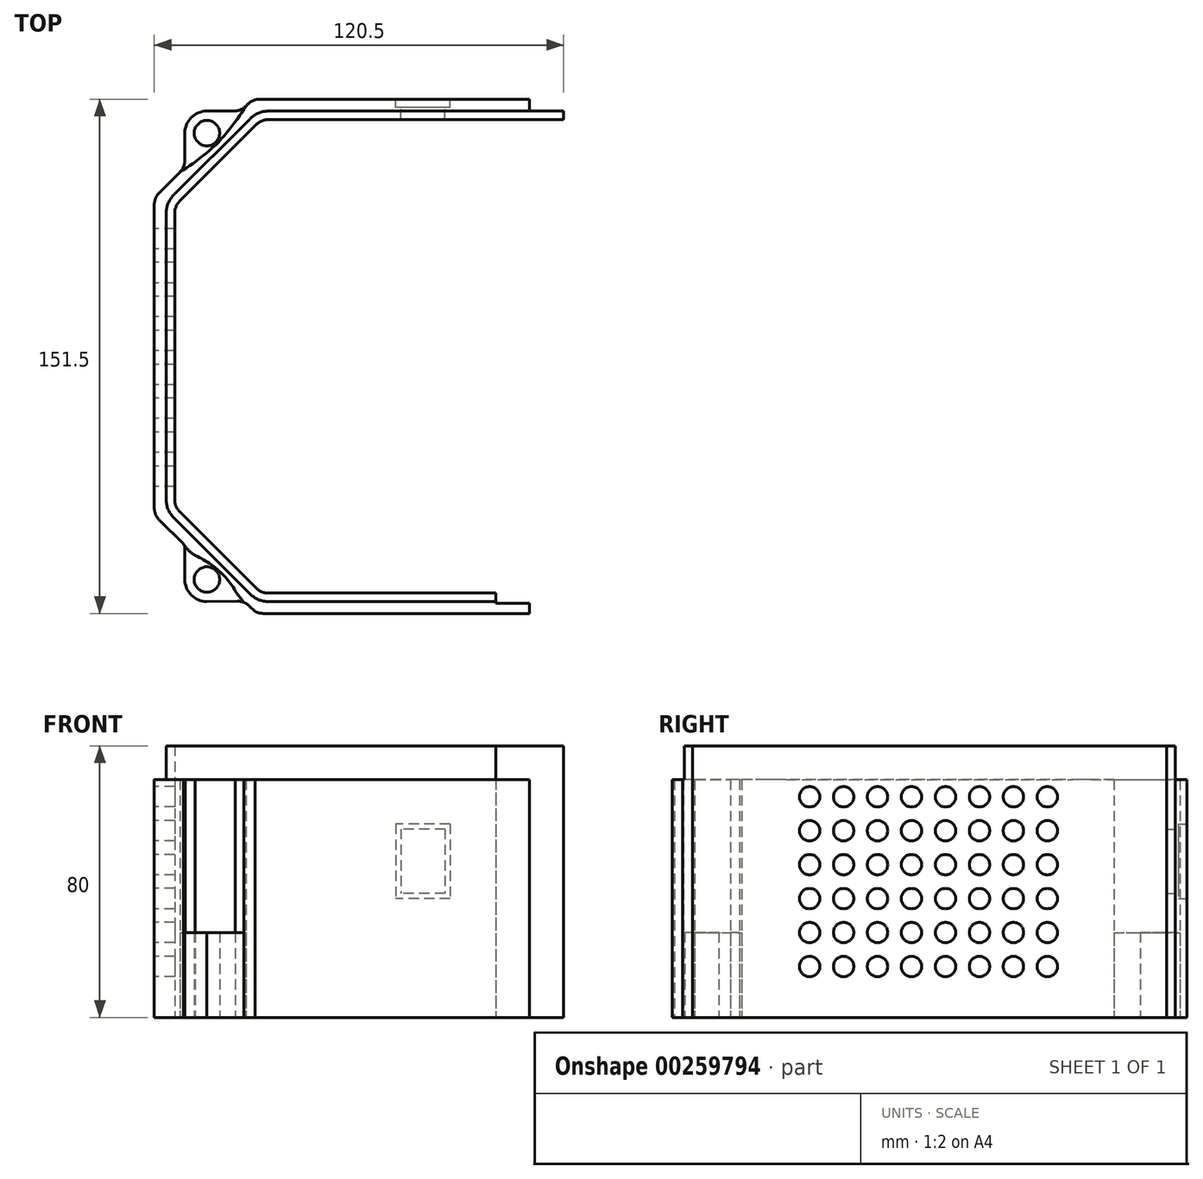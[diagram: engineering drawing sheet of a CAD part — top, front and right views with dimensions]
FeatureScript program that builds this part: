
annotation { "Feature Type Name" : "Feature", "Feature Type Description" : "" }
export const myFeature = defineFeature(function(context is Context, id is Id, definition is map)
    precondition{}
    {
        {
            var Q0;
            Q0=qCreatedBy(makeId("Top.planeOp"),FACE);
            var sketch = newSketch(context, id + "F0", { "sketchPlane" : qUnion([Q0])});
            skLineSegment(sketch, "E0.bottom", {"start": v(-49.42, 75.75) * mm, "end": v(30, 75.75) * mm});
            skLineSegment(sketch, "E0.top", {"start": v(-48.4, -75.75) * mm, "end": v(30, -75.75) * mm});
            skLineSegment(sketch, "E0.left", {"start": v(-80.5, 44.67) * mm, "end": v(-80.5, -44.67) * mm});
            skLineSegment(sketch, "E0.right", {"start": v(30, 75.75) * mm, "end": v(30, 72.25) * mm});
            skCircle(sketch, "E1", {"center": v(-65, 65.75) * mm, "radius": 3.75 * mm});
            skCircle(sketch, "E2", {"center": v(-65, -65.75) * mm, "radius": 3.75 * mm});
            skPoint(sketch, "E3.visualSharp", {"position": v(-80.5, 75.75) * mm});
            skPoint(sketch, "E4.visualSharp", {"position": v(-80.5, -75.75) * mm});
            skLineSegment(sketch, "E5.0", {"start": v(-46.93, 69.75) * mm, "end": v(30, 69.75) * mm});
            skLineSegment(sketch, "E6.trimOffspring", {"start": v(30, -72.75) * mm, "end": v(30, -75.75) * mm});
            skLineSegment(sketch, "E7", {"start": v(-73.04, 45.72) * mm, "end": v(-50.47, 68.29) * mm});
            skLineSegment(sketch, "E8", {"start": v(-73.04, -45.72) * mm, "end": v(-50.47, -68.29) * mm});
            skLineSegment(sketch, "E9.trimOffspring", {"start": v(-46.94, -69.75) * mm, "end": v(20, -69.75) * mm});
            skArc(sketch, "E10.trimOffspring", {"start": v(-60.05, -58.7) * mm, "mid": v(-60.25, -58.5) * mm, "end": v(-60.46, -58.3) * mm, "construction": true});
            skArc(sketch, "E11", {"start": v(-71.5, -65.75) * mm, "mid": v(-69.6, -70.35) * mm, "end": v(-65, -72.25) * mm});
            skArc(sketch, "E12", {"start": v(-65, 72.25) * mm, "mid": v(-69.6, 70.35) * mm, "end": v(-71.5, 65.75) * mm});
            skPoint(sketch, "E13.visualSharp", {"position": v(-49, -69.75) * mm});
            skArc(sketch, "E13.filletArc", {"start": v(-50.47, -68.29) * mm, "mid": v(-48.85, -69.37) * mm, "end": v(-46.94, -69.75) * mm});
            skPoint(sketch, "E14.visualSharp", {"position": v(-74.5, -44.26) * mm});
            skArc(sketch, "E14.filletArc", {"start": v(-74.5, -42.19) * mm, "mid": v(-74.12, -44.1) * mm, "end": v(-73.04, -45.72) * mm});
            skPoint(sketch, "E15.visualSharp", {"position": v(-74.5, 44.25) * mm});
            skArc(sketch, "E15.filletArc", {"start": v(-73.04, 45.72) * mm, "mid": v(-74.12, 44.1) * mm, "end": v(-74.5, 42.18) * mm});
            skPoint(sketch, "E16.visualSharp", {"position": v(-49, 69.75) * mm});
            skArc(sketch, "E16.filletArc", {"start": v(-46.93, 69.75) * mm, "mid": v(-48.85, 69.37) * mm, "end": v(-50.47, 68.29) * mm});
            skLineSegment(sketch, "E17", {"start": v(-79.04, -48.2) * mm, "end": v(-71.96, -55.28) * mm});
            skPoint(sketch, "E18.visualSharp", {"position": v(-70.5, -56.75) * mm});
            skArc(sketch, "E19.filletArc", {"start": v(-80.5, -44.67) * mm, "mid": v(-80.12, -46.59) * mm, "end": v(-79.04, -48.2) * mm});
            skPoint(sketch, "E20.visualSharp", {"position": v(-56, -71.25) * mm});
            skPoint(sketch, "E21.visualSharp", {"position": v(-51.5, -75.75) * mm});
            skArc(sketch, "E21.filletArc", {"start": v(-50.86, -75.1) * mm, "mid": v(-49.68, -75.59) * mm, "end": v(-48.4, -75.75) * mm});
            skLineSegment(sketch, "E22", {"start": v(-65, 72.25) * mm, "end": v(-57.06, 72.25) * mm});
            skLineSegment(sketch, "E23", {"start": v(-71.5, 57.81) * mm, "end": v(-71.5, 65.75) * mm});
            skLineSegment(sketch, "E24", {"start": v(-72.96, 54.28) * mm, "end": v(-79.04, 48.2) * mm});
            skLineSegment(sketch, "E25", {"start": v(-53.53, 73.71) * mm, "end": v(-52.95, 74.29) * mm});
            skPoint(sketch, "E26.visualSharp", {"position": v(-80.5, 46.74) * mm});
            skArc(sketch, "E26.filletArc", {"start": v(-79.04, 48.2) * mm, "mid": v(-80.12, 46.58) * mm, "end": v(-80.5, 44.67) * mm});
            skPoint(sketch, "E27.visualSharp", {"position": v(-71.5, 55.74) * mm});
            skArc(sketch, "E27.filletArc", {"start": v(-72.96, 54.28) * mm, "mid": v(-71.88, 55.9) * mm, "end": v(-71.5, 57.81) * mm});
            skPoint(sketch, "E28.visualSharp", {"position": v(-54.99, 72.25) * mm});
            skArc(sketch, "E28.filletArc", {"start": v(-57.06, 72.25) * mm, "mid": v(-55.15, 72.63) * mm, "end": v(-53.53, 73.71) * mm});
            skPoint(sketch, "E29.visualSharp", {"position": v(-51.49, 75.75) * mm});
            skArc(sketch, "E29.filletArc", {"start": v(-49.42, 75.75) * mm, "mid": v(-51.33, 75.37) * mm, "end": v(-52.95, 74.29) * mm});
            skLineSegment(sketch, "E30", {"start": v(-74.5, -42.19) * mm, "end": v(-74.5, 42.18) * mm});
            skLineSegment(sketch, "E31", {"start": v(-59, -59.75) * mm, "end": v(-80.03, -80.78) * mm, "construction": true});
            skArc(sketch, "E32.filletArc", {"start": v(-71.36, -56.02) * mm, "mid": v(-70.06, -57.5) * mm, "end": v(-68.44, -58.62) * mm});
            skPoint(sketch, "E33.orphan", {"position": v(-62.35, -63.1) * mm});
            skPoint(sketch, "E34.orphan", {"position": v(-56, -69.45) * mm});
            skPoint(sketch, "E35.orphan", {"position": v(-68.7, -56.75) * mm});
            skPoint(sketch, "E36", {"position": v(-62, -62.74) * mm});
            skFitSpline(sketch, "E37", {"points": [v(-56.66, -69.17) * mm, v(-62, -62.74) * mm, v(-68.44, -58.62) * mm], "startDerivative": vector(-7.08, 14.05) * mm, "endDerivative": vector(-14.05, 7.08) * mm});
            skLineSegment(sketch, "E38", {"start": v(-62, 62.74) * mm, "end": v(-62.35, 63.1) * mm, "construction": true});
            skPoint(sketch, "E39", {"position": v(-62, 62.74) * mm});
            skFitSpline(sketch, "E40", {"points": [v(-72.96, 54.28) * mm, v(-62, 62.74) * mm, v(-53.53, 73.71) * mm], "startDerivative": vector(21.19, 13.69) * mm, "endDerivative": vector(13.69, 21.19) * mm});
            skLineSegment(sketch, "E41.trimOffspring", {"start": v(-67.65, 68.4) * mm, "end": v(-69.6, 70.35) * mm, "construction": true});
            skLineSegment(sketch, "E42", {"start": v(-71.97, -55.28) * mm, "end": v(-71.96, -55.28) * mm});
            skLineSegment(sketch, "E43", {"start": v(-71.5, -65.75) * mm, "end": v(-71.5, -56.56) * mm});
            skLineSegment(sketch, "E44", {"start": v(-65, -72.25) * mm, "end": v(-56.04, -72.14) * mm});
            skArc(sketch, "E45.filletArc", {"start": v(-71.5, -56.56) * mm, "mid": v(-71.62, -55.88) * mm, "end": v(-71.97, -55.28) * mm});
            skLineSegment(sketch, "E46", {"start": v(-50.86, -75.1) * mm, "end": v(-52.55, -73.51) * mm});
            skPoint(sketch, "E47.visualSharp", {"position": v(-54.02, -72.12) * mm});
            skArc(sketch, "E47.filletArc", {"start": v(-52.55, -73.51) * mm, "mid": v(-54.16, -72.49) * mm, "end": v(-56.04, -72.14) * mm});
            skLineSegment(sketch, "E48", {"start": v(-56.66, -69.17) * mm, "end": v(-54.16, -72.49) * mm});
            skLineSegment(sketch, "E49", {"start": v(-71.36, -56.02) * mm, "end": v(-71.96, -55.28) * mm});
            skLineSegment(sketch, "E50.bottom", {"start": v(30, 69.75) * mm, "end": v(40, 69.75) * mm});
            skLineSegment(sketch, "E50.top", {"start": v(30, 72.25) * mm, "end": v(40, 72.25) * mm});
            skLineSegment(sketch, "E50.right", {"start": v(40, 69.75) * mm, "end": v(40, 72.25) * mm});
            skLineSegment(sketch, "E51.top", {"start": v(20, -72.75) * mm, "end": v(30, -72.75) * mm});
            skLineSegment(sketch, "E51.left", {"start": v(20, -69.75) * mm, "end": v(20, -72.75) * mm});
            skSolve(sketch);
        }
        {
            var Q0;
            Q0=makeQuery(id+"F0.imprint","IMPRINT",FACE,{"disambiguationData":[TD([[makeQuery(id+"F0.imprint","IMPRINT",EDGE,{"derivedFrom":sQuery(id+"F0.wireOp",EDGE,"E2")}),-1.0]])]});
            var Q1;
            Q1=makeQuery(id+"F0.imprint","IMPRINT",FACE,{"disambiguationData":[TD([[makeQuery(id+"F0.imprint","IMPRINT",EDGE,{"derivedFrom":sQuery(id+"F0.wireOp",EDGE,"E1")}),-1.0]])]});
            extrude(context, id + "F1", {"entities" : qUnion([Q0, Q1]), "depth" : 25 * mm});
        }
        {
            var Q0;
            Q0=makeQuery(id+"F0.imprint","IMPRINT",FACE,{"disambiguationData":[TD([[makeQuery(id+"F0.imprint","IMPRINT",EDGE,{"derivedFrom":sQuery(id+"F0.wireOp",EDGE,"E0.bottom")}),-1.0]])]});
            extrude(context, id + "F2", {"entities" : qUnion([Q0]), "depth" : 70 * mm});
        }
        {
            var Q0;
            Q0=makeQuery(id+"F2.opExtrude","CAP_FACE",FACE,{"disambiguationData":[OSD([sQuery(id+"F0.wireOp",EDGE,"E0.bottom"),sQuery(id+"F0.wireOp",EDGE,"E0.top"),sQuery(id+"F0.wireOp",EDGE,"E0.left"),sQuery(id+"F0.wireOp",EDGE,"E0.right"),sQuery(id+"F0.wireOp",EDGE,"E5.0"),sQuery(id+"F0.wireOp",EDGE,"E6.trimOffspring"),sQuery(id+"F0.wireOp",EDGE,"E7"),sQuery(id+"F0.wireOp",EDGE,"E8"),sQuery(id+"F0.wireOp",EDGE,"E9.trimOffspring"),sQuery(id+"F0.wireOp",EDGE,"E13.filletArc"),sQuery(id+"F0.wireOp",EDGE,"E14.filletArc"),sQuery(id+"F0.wireOp",EDGE,"E15.filletArc"),sQuery(id+"F0.wireOp",EDGE,"E16.filletArc"),sQuery(id+"F0.wireOp",EDGE,"E17"),sQuery(id+"F0.wireOp",EDGE,"E19.filletArc"),sQuery(id+"F0.wireOp",EDGE,"E21.filletArc"),sQuery(id+"F0.wireOp",EDGE,"E24"),sQuery(id+"F0.wireOp",EDGE,"E25"),sQuery(id+"F0.wireOp",EDGE,"E26.filletArc"),sQuery(id+"F0.wireOp",EDGE,"E29.filletArc"),sQuery(id+"F0.wireOp",EDGE,"E30"),sQuery(id+"F0.wireOp",EDGE,"E32.filletArc"),sQuery(id+"F0.wireOp",EDGE,"E37"),sQuery(id+"F0.wireOp",EDGE,"E40"),sQuery(id+"F0.wireOp",EDGE,"E46"),sQuery(id+"F0.wireOp",EDGE,"E47.filletArc"),sQuery(id+"F0.wireOp",EDGE,"E48"),sQuery(id+"F0.wireOp",EDGE,"E49"),sQuery(id+"F0.wireOp",EDGE,"E50.bottom"),sQuery(id+"F0.wireOp",EDGE,"E50.top"),sQuery(id+"F0.wireOp",EDGE,"E50.right"),sQuery(id+"F0.wireOp",EDGE,"E51.top"),sQuery(id+"F0.wireOp",EDGE,"E51.left")])],"isStart":false});
            var sketch = newSketch(context, id + "F3", { "sketchPlane" : qUnion([Q0])});
            skLineSegment(sketch, "E52.0", {"start": v(-46.94, -72.25) * mm, "end": v(20, -72.25) * mm});
            skArc(sketch, "E52.1", {"start": v(-52.24, -70.05) * mm, "mid": v(-49.8, -71.68) * mm, "end": v(-46.94, -72.25) * mm});
            skLineSegment(sketch, "E52.2", {"start": v(-74.8, -47.5) * mm, "end": v(-52.24, -70.05) * mm});
            skArc(sketch, "E52.3", {"start": v(-77, -42.19) * mm, "mid": v(-76.43, -45.06) * mm, "end": v(-74.8, -47.5) * mm});
            skLineSegment(sketch, "E52.4", {"start": v(-77, -42.19) * mm, "end": v(-77, 42.18) * mm});
            skArc(sketch, "E52.5", {"start": v(-74.8, 47.49) * mm, "mid": v(-76.43, 45.05) * mm, "end": v(-77, 42.18) * mm});
            skLineSegment(sketch, "E52.6", {"start": v(30, 72.25) * mm, "end": v(40, 72.25) * mm});
            skLineSegment(sketch, "E52.7", {"start": v(-46.93, 72.25) * mm, "end": v(30, 72.25) * mm});
            skArc(sketch, "E52.8", {"start": v(-46.93, 72.25) * mm, "mid": v(-49.8, 71.68) * mm, "end": v(-52.24, 70.05) * mm});
            skLineSegment(sketch, "E52.9", {"start": v(-74.8, 47.49) * mm, "end": v(-52.24, 70.05) * mm});
            skLineSegment(sketch, "E53", {"start": v(20, -72.25) * mm, "end": v(20, -69.75) * mm});
            skLineSegment(sketch, "E54", {"start": v(40, 69.75) * mm, "end": v(40, 72.25) * mm});
            skSolve(sketch);
        }
        {
            var Q0;
            Q0=makeQuery(id+"F3.imprint","IMPRINT",FACE,{"disambiguationData":[TD([[makeQuery(id+"F3.imprint","IMPRINT",EDGE,{"derivedFrom":sQuery(id+"F3.wireOp",EDGE,"E52.0")}),1.0]])]});
            extrude(context, id + "F4", {"entities" : qUnion([Q0]), "operationType" : NewBodyOperationType.ADD, "depth" : 10 * mm});
        }
        {
            var Q0;
            Q0=makeQuery(id+"F2.opExtrude","SWEPT_FACE",FACE,{"disambiguationData":[OSD([sQuery(id+"F0.wireOp",EDGE,"E0.left")])]});
            var sketch = newSketch(context, id + "F5", { "sketchPlane" : qUnion([Q0])});
            skCircle(sketch, "E55", {"center": v(-34.67, 15) * mm, "radius": 3 * mm});
            skCircle(sketch, "E56.0.1.0", {"center": v(-34.67, 25) * mm, "radius": 3 * mm});
            skCircle(sketch, "E56.0.2.0", {"center": v(-34.67, 35) * mm, "radius": 3 * mm});
            skCircle(sketch, "E56.0.3.0", {"center": v(-34.67, 45) * mm, "radius": 3 * mm});
            skCircle(sketch, "E56.0.4.0", {"center": v(-34.67, 55) * mm, "radius": 3 * mm});
            skCircle(sketch, "E56.0.5.0", {"center": v(-34.67, 65) * mm, "radius": 3 * mm});
            skCircle(sketch, "E56.1.0.0", {"center": v(-24.67, 15) * mm, "radius": 3 * mm});
            skCircle(sketch, "E56.1.1.0", {"center": v(-24.67, 25) * mm, "radius": 3 * mm});
            skCircle(sketch, "E56.1.2.0", {"center": v(-24.67, 35) * mm, "radius": 3 * mm});
            skCircle(sketch, "E56.1.3.0", {"center": v(-24.67, 45) * mm, "radius": 3 * mm});
            skCircle(sketch, "E56.1.4.0", {"center": v(-24.67, 55) * mm, "radius": 3 * mm});
            skCircle(sketch, "E56.1.5.0", {"center": v(-24.67, 65) * mm, "radius": 3 * mm});
            skCircle(sketch, "E56.2.0.0", {"center": v(-14.67, 15) * mm, "radius": 3 * mm});
            skCircle(sketch, "E56.2.1.0", {"center": v(-14.67, 25) * mm, "radius": 3 * mm});
            skCircle(sketch, "E56.2.2.0", {"center": v(-14.67, 35) * mm, "radius": 3 * mm});
            skCircle(sketch, "E56.2.3.0", {"center": v(-14.67, 45) * mm, "radius": 3 * mm});
            skCircle(sketch, "E56.2.4.0", {"center": v(-14.67, 55) * mm, "radius": 3 * mm});
            skCircle(sketch, "E56.2.5.0", {"center": v(-14.67, 65) * mm, "radius": 3 * mm});
            skCircle(sketch, "E56.3.0.0", {"center": v(-4.67, 15) * mm, "radius": 3 * mm});
            skCircle(sketch, "E56.3.1.0", {"center": v(-4.67, 25) * mm, "radius": 3 * mm});
            skCircle(sketch, "E56.3.2.0", {"center": v(-4.67, 35) * mm, "radius": 3 * mm});
            skCircle(sketch, "E56.3.3.0", {"center": v(-4.67, 45) * mm, "radius": 3 * mm});
            skCircle(sketch, "E56.3.4.0", {"center": v(-4.67, 55) * mm, "radius": 3 * mm});
            skCircle(sketch, "E56.3.5.0", {"center": v(-4.67, 65) * mm, "radius": 3 * mm});
            skCircle(sketch, "E56.4.0.0", {"center": v(5.33, 15) * mm, "radius": 3 * mm});
            skCircle(sketch, "E56.4.1.0", {"center": v(5.33, 25) * mm, "radius": 3 * mm});
            skCircle(sketch, "E56.4.2.0", {"center": v(5.33, 35) * mm, "radius": 3 * mm});
            skCircle(sketch, "E56.4.3.0", {"center": v(5.33, 45) * mm, "radius": 3 * mm});
            skCircle(sketch, "E56.4.4.0", {"center": v(5.33, 55) * mm, "radius": 3 * mm});
            skCircle(sketch, "E56.4.5.0", {"center": v(5.33, 65) * mm, "radius": 3 * mm});
            skCircle(sketch, "E56.5.0.0", {"center": v(15.33, 15) * mm, "radius": 3 * mm});
            skCircle(sketch, "E56.5.1.0", {"center": v(15.33, 25) * mm, "radius": 3 * mm});
            skCircle(sketch, "E56.5.2.0", {"center": v(15.33, 35) * mm, "radius": 3 * mm});
            skCircle(sketch, "E56.5.3.0", {"center": v(15.33, 45) * mm, "radius": 3 * mm});
            skCircle(sketch, "E56.5.4.0", {"center": v(15.33, 55) * mm, "radius": 3 * mm});
            skCircle(sketch, "E56.5.5.0", {"center": v(15.33, 65) * mm, "radius": 3 * mm});
            skCircle(sketch, "E56.6.0.0", {"center": v(25.33, 15) * mm, "radius": 3 * mm});
            skCircle(sketch, "E56.6.1.0", {"center": v(25.33, 25) * mm, "radius": 3 * mm});
            skCircle(sketch, "E56.6.2.0", {"center": v(25.33, 35) * mm, "radius": 3 * mm});
            skCircle(sketch, "E56.6.3.0", {"center": v(25.33, 45) * mm, "radius": 3 * mm});
            skCircle(sketch, "E56.6.4.0", {"center": v(25.33, 55) * mm, "radius": 3 * mm});
            skCircle(sketch, "E56.6.5.0", {"center": v(25.33, 65) * mm, "radius": 3 * mm});
            skCircle(sketch, "E56.7.0.0", {"center": v(35.33, 15) * mm, "radius": 3 * mm});
            skCircle(sketch, "E56.7.1.0", {"center": v(35.33, 25) * mm, "radius": 3 * mm});
            skCircle(sketch, "E56.7.2.0", {"center": v(35.33, 35) * mm, "radius": 3 * mm});
            skCircle(sketch, "E56.7.3.0", {"center": v(35.33, 45) * mm, "radius": 3 * mm});
            skCircle(sketch, "E56.7.4.0", {"center": v(35.33, 55) * mm, "radius": 3 * mm});
            skCircle(sketch, "E56.7.5.0", {"center": v(35.33, 65) * mm, "radius": 3 * mm});
            skLineSegment(sketch, "E56.direction1", {"start": v(-34.67, 15) * mm, "end": v(-24.67, 15) * mm, "construction": true});
            skLineSegment(sketch, "E56.direction2", {"start": v(-34.67, 15) * mm, "end": v(-34.67, 25) * mm, "construction": true});
            skSolve(sketch);
        }
        {
            var Q0;
            Q0=makeQuery(id+"F5.imprint","IMPRINT",FACE,{"disambiguationData":[TD([[makeQuery(id+"F5.imprint","IMPRINT",EDGE,{"derivedFrom":sQuery(id+"F5.wireOp",EDGE,"E56.1.5.0")}),1.0]])]});
            var Q1;
            Q1=makeQuery(id+"F5.imprint","IMPRINT",FACE,{"disambiguationData":[TD([[makeQuery(id+"F5.imprint","IMPRINT",EDGE,{"derivedFrom":sQuery(id+"F5.wireOp",EDGE,"E56.0.5.0")}),1.0]])]});
            var Q2;
            Q2=makeQuery(id+"F5.imprint","IMPRINT",FACE,{"disambiguationData":[TD([[makeQuery(id+"F5.imprint","IMPRINT",EDGE,{"derivedFrom":sQuery(id+"F5.wireOp",EDGE,"E56.2.5.0")}),1.0]])]});
            var Q3;
            Q3=makeQuery(id+"F5.imprint","IMPRINT",FACE,{"disambiguationData":[TD([[makeQuery(id+"F5.imprint","IMPRINT",EDGE,{"derivedFrom":sQuery(id+"F5.wireOp",EDGE,"E56.3.5.0")}),1.0]])]});
            var Q4;
            Q4=makeQuery(id+"F5.imprint","IMPRINT",FACE,{"disambiguationData":[TD([[makeQuery(id+"F5.imprint","IMPRINT",EDGE,{"derivedFrom":sQuery(id+"F5.wireOp",EDGE,"E56.4.5.0")}),1.0]])]});
            var Q5;
            Q5=makeQuery(id+"F5.imprint","IMPRINT",FACE,{"disambiguationData":[TD([[makeQuery(id+"F5.imprint","IMPRINT",EDGE,{"derivedFrom":sQuery(id+"F5.wireOp",EDGE,"E56.5.5.0")}),1.0]])]});
            var Q6;
            Q6=makeQuery(id+"F5.imprint","IMPRINT",FACE,{"disambiguationData":[TD([[makeQuery(id+"F5.imprint","IMPRINT",EDGE,{"derivedFrom":sQuery(id+"F5.wireOp",EDGE,"E56.6.5.0")}),1.0]])]});
            var Q7;
            Q7=makeQuery(id+"F5.imprint","IMPRINT",FACE,{"disambiguationData":[TD([[makeQuery(id+"F5.imprint","IMPRINT",EDGE,{"derivedFrom":sQuery(id+"F5.wireOp",EDGE,"E56.7.5.0")}),1.0]])]});
            var Q8;
            Q8=makeQuery(id+"F5.imprint","IMPRINT",FACE,{"disambiguationData":[TD([[makeQuery(id+"F5.imprint","IMPRINT",EDGE,{"derivedFrom":sQuery(id+"F5.wireOp",EDGE,"E56.7.4.0")}),1.0]])]});
            var Q9;
            Q9=makeQuery(id+"F5.imprint","IMPRINT",FACE,{"disambiguationData":[TD([[makeQuery(id+"F5.imprint","IMPRINT",EDGE,{"derivedFrom":sQuery(id+"F5.wireOp",EDGE,"E56.6.4.0")}),1.0]])]});
            var Q10;
            Q10=makeQuery(id+"F5.imprint","IMPRINT",FACE,{"disambiguationData":[TD([[makeQuery(id+"F5.imprint","IMPRINT",EDGE,{"derivedFrom":sQuery(id+"F5.wireOp",EDGE,"E56.5.4.0")}),1.0]])]});
            var Q11;
            Q11=makeQuery(id+"F5.imprint","IMPRINT",FACE,{"disambiguationData":[TD([[makeQuery(id+"F5.imprint","IMPRINT",EDGE,{"derivedFrom":sQuery(id+"F5.wireOp",EDGE,"E56.4.4.0")}),1.0]])]});
            var Q12;
            Q12=makeQuery(id+"F5.imprint","IMPRINT",FACE,{"disambiguationData":[TD([[makeQuery(id+"F5.imprint","IMPRINT",EDGE,{"derivedFrom":sQuery(id+"F5.wireOp",EDGE,"E56.3.4.0")}),1.0]])]});
            var Q13;
            Q13=makeQuery(id+"F5.imprint","IMPRINT",FACE,{"disambiguationData":[TD([[makeQuery(id+"F5.imprint","IMPRINT",EDGE,{"derivedFrom":sQuery(id+"F5.wireOp",EDGE,"E56.2.4.0")}),1.0]])]});
            var Q14;
            Q14=makeQuery(id+"F5.imprint","IMPRINT",FACE,{"disambiguationData":[TD([[makeQuery(id+"F5.imprint","IMPRINT",EDGE,{"derivedFrom":sQuery(id+"F5.wireOp",EDGE,"E56.1.4.0")}),1.0]])]});
            var Q15;
            Q15=makeQuery(id+"F5.imprint","IMPRINT",FACE,{"disambiguationData":[TD([[makeQuery(id+"F5.imprint","IMPRINT",EDGE,{"derivedFrom":sQuery(id+"F5.wireOp",EDGE,"E56.0.4.0")}),1.0]])]});
            var Q16;
            Q16=makeQuery(id+"F5.imprint","IMPRINT",FACE,{"disambiguationData":[TD([[makeQuery(id+"F5.imprint","IMPRINT",EDGE,{"derivedFrom":sQuery(id+"F5.wireOp",EDGE,"E56.0.3.0")}),1.0]])]});
            var Q17;
            Q17=makeQuery(id+"F5.imprint","IMPRINT",FACE,{"disambiguationData":[TD([[makeQuery(id+"F5.imprint","IMPRINT",EDGE,{"derivedFrom":sQuery(id+"F5.wireOp",EDGE,"E56.1.3.0")}),1.0]])]});
            var Q18;
            Q18=makeQuery(id+"F5.imprint","IMPRINT",FACE,{"disambiguationData":[TD([[makeQuery(id+"F5.imprint","IMPRINT",EDGE,{"derivedFrom":sQuery(id+"F5.wireOp",EDGE,"E56.2.3.0")}),1.0]])]});
            var Q19;
            Q19=makeQuery(id+"F5.imprint","IMPRINT",FACE,{"disambiguationData":[TD([[makeQuery(id+"F5.imprint","IMPRINT",EDGE,{"derivedFrom":sQuery(id+"F5.wireOp",EDGE,"E56.3.3.0")}),1.0]])]});
            var Q20;
            Q20=makeQuery(id+"F5.imprint","IMPRINT",FACE,{"disambiguationData":[TD([[makeQuery(id+"F5.imprint","IMPRINT",EDGE,{"derivedFrom":sQuery(id+"F5.wireOp",EDGE,"E56.4.3.0")}),1.0]])]});
            var Q21;
            Q21=makeQuery(id+"F5.imprint","IMPRINT",FACE,{"disambiguationData":[TD([[makeQuery(id+"F5.imprint","IMPRINT",EDGE,{"derivedFrom":sQuery(id+"F5.wireOp",EDGE,"E56.5.3.0")}),1.0]])]});
            var Q22;
            Q22=makeQuery(id+"F5.imprint","IMPRINT",FACE,{"disambiguationData":[TD([[makeQuery(id+"F5.imprint","IMPRINT",EDGE,{"derivedFrom":sQuery(id+"F5.wireOp",EDGE,"E56.6.3.0")}),1.0]])]});
            var Q23;
            Q23=makeQuery(id+"F5.imprint","IMPRINT",FACE,{"disambiguationData":[TD([[makeQuery(id+"F5.imprint","IMPRINT",EDGE,{"derivedFrom":sQuery(id+"F5.wireOp",EDGE,"E56.7.3.0")}),1.0]])]});
            var Q24;
            Q24=makeQuery(id+"F5.imprint","IMPRINT",FACE,{"disambiguationData":[TD([[makeQuery(id+"F5.imprint","IMPRINT",EDGE,{"derivedFrom":sQuery(id+"F5.wireOp",EDGE,"E56.7.2.0")}),1.0]])]});
            var Q25;
            Q25=makeQuery(id+"F5.imprint","IMPRINT",FACE,{"disambiguationData":[TD([[makeQuery(id+"F5.imprint","IMPRINT",EDGE,{"derivedFrom":sQuery(id+"F5.wireOp",EDGE,"E56.6.2.0")}),1.0]])]});
            var Q26;
            Q26=makeQuery(id+"F5.imprint","IMPRINT",FACE,{"disambiguationData":[TD([[makeQuery(id+"F5.imprint","IMPRINT",EDGE,{"derivedFrom":sQuery(id+"F5.wireOp",EDGE,"E56.5.2.0")}),1.0]])]});
            var Q27;
            Q27=makeQuery(id+"F5.imprint","IMPRINT",FACE,{"disambiguationData":[TD([[makeQuery(id+"F5.imprint","IMPRINT",EDGE,{"derivedFrom":sQuery(id+"F5.wireOp",EDGE,"E56.4.2.0")}),1.0]])]});
            var Q28;
            Q28=makeQuery(id+"F5.imprint","IMPRINT",FACE,{"disambiguationData":[TD([[makeQuery(id+"F5.imprint","IMPRINT",EDGE,{"derivedFrom":sQuery(id+"F5.wireOp",EDGE,"E56.3.2.0")}),1.0]])]});
            var Q29;
            Q29=makeQuery(id+"F5.imprint","IMPRINT",FACE,{"disambiguationData":[TD([[makeQuery(id+"F5.imprint","IMPRINT",EDGE,{"derivedFrom":sQuery(id+"F5.wireOp",EDGE,"E56.2.2.0")}),1.0]])]});
            var Q30;
            Q30=makeQuery(id+"F5.imprint","IMPRINT",FACE,{"disambiguationData":[TD([[makeQuery(id+"F5.imprint","IMPRINT",EDGE,{"derivedFrom":sQuery(id+"F5.wireOp",EDGE,"E56.1.2.0")}),1.0]])]});
            var Q31;
            Q31=makeQuery(id+"F5.imprint","IMPRINT",FACE,{"disambiguationData":[TD([[makeQuery(id+"F5.imprint","IMPRINT",EDGE,{"derivedFrom":sQuery(id+"F5.wireOp",EDGE,"E56.0.2.0")}),1.0]])]});
            var Q32;
            Q32=makeQuery(id+"F5.imprint","IMPRINT",FACE,{"disambiguationData":[TD([[makeQuery(id+"F5.imprint","IMPRINT",EDGE,{"derivedFrom":sQuery(id+"F5.wireOp",EDGE,"E56.0.1.0")}),1.0]])]});
            var Q33;
            Q33=makeQuery(id+"F5.imprint","IMPRINT",FACE,{"disambiguationData":[TD([[makeQuery(id+"F5.imprint","IMPRINT",EDGE,{"derivedFrom":sQuery(id+"F5.wireOp",EDGE,"E56.1.1.0")}),1.0]])]});
            var Q34;
            Q34=makeQuery(id+"F5.imprint","IMPRINT",FACE,{"disambiguationData":[TD([[makeQuery(id+"F5.imprint","IMPRINT",EDGE,{"derivedFrom":sQuery(id+"F5.wireOp",EDGE,"E56.2.1.0")}),1.0]])]});
            var Q35;
            Q35=makeQuery(id+"F5.imprint","IMPRINT",FACE,{"disambiguationData":[TD([[makeQuery(id+"F5.imprint","IMPRINT",EDGE,{"derivedFrom":sQuery(id+"F5.wireOp",EDGE,"E56.3.1.0")}),1.0]])]});
            var Q36;
            Q36=makeQuery(id+"F5.imprint","IMPRINT",FACE,{"disambiguationData":[TD([[makeQuery(id+"F5.imprint","IMPRINT",EDGE,{"derivedFrom":sQuery(id+"F5.wireOp",EDGE,"E56.4.1.0")}),1.0]])]});
            var Q37;
            Q37=makeQuery(id+"F5.imprint","IMPRINT",FACE,{"disambiguationData":[TD([[makeQuery(id+"F5.imprint","IMPRINT",EDGE,{"derivedFrom":sQuery(id+"F5.wireOp",EDGE,"E56.5.1.0")}),1.0]])]});
            var Q38;
            Q38=makeQuery(id+"F5.imprint","IMPRINT",FACE,{"disambiguationData":[TD([[makeQuery(id+"F5.imprint","IMPRINT",EDGE,{"derivedFrom":sQuery(id+"F5.wireOp",EDGE,"E56.6.1.0")}),1.0]])]});
            var Q39;
            Q39=makeQuery(id+"F5.imprint","IMPRINT",FACE,{"disambiguationData":[TD([[makeQuery(id+"F5.imprint","IMPRINT",EDGE,{"derivedFrom":sQuery(id+"F5.wireOp",EDGE,"E56.7.1.0")}),1.0]])]});
            var Q40;
            Q40=makeQuery(id+"F5.imprint","IMPRINT",FACE,{"disambiguationData":[TD([[makeQuery(id+"F5.imprint","IMPRINT",EDGE,{"derivedFrom":sQuery(id+"F5.wireOp",EDGE,"E56.7.0.0")}),1.0]])]});
            var Q41;
            Q41=makeQuery(id+"F5.imprint","IMPRINT",FACE,{"disambiguationData":[TD([[makeQuery(id+"F5.imprint","IMPRINT",EDGE,{"derivedFrom":sQuery(id+"F5.wireOp",EDGE,"E56.6.0.0")}),1.0]])]});
            var Q42;
            Q42=makeQuery(id+"F5.imprint","IMPRINT",FACE,{"disambiguationData":[TD([[makeQuery(id+"F5.imprint","IMPRINT",EDGE,{"derivedFrom":sQuery(id+"F5.wireOp",EDGE,"E56.5.0.0")}),1.0]])]});
            var Q43;
            Q43=makeQuery(id+"F5.imprint","IMPRINT",FACE,{"disambiguationData":[TD([[makeQuery(id+"F5.imprint","IMPRINT",EDGE,{"derivedFrom":sQuery(id+"F5.wireOp",EDGE,"E56.4.0.0")}),1.0]])]});
            var Q44;
            Q44=makeQuery(id+"F5.imprint","IMPRINT",FACE,{"disambiguationData":[TD([[makeQuery(id+"F5.imprint","IMPRINT",EDGE,{"derivedFrom":sQuery(id+"F5.wireOp",EDGE,"E56.3.0.0")}),1.0]])]});
            var Q45;
            Q45=makeQuery(id+"F5.imprint","IMPRINT",FACE,{"disambiguationData":[TD([[makeQuery(id+"F5.imprint","IMPRINT",EDGE,{"derivedFrom":sQuery(id+"F5.wireOp",EDGE,"E56.2.0.0")}),1.0]])]});
            var Q46;
            Q46=makeQuery(id+"F5.imprint","IMPRINT",FACE,{"disambiguationData":[TD([[makeQuery(id+"F5.imprint","IMPRINT",EDGE,{"derivedFrom":sQuery(id+"F5.wireOp",EDGE,"E56.1.0.0")}),1.0]])]});
            var Q47;
            Q47=makeQuery(id+"F5.imprint","IMPRINT",FACE,{"disambiguationData":[TD([[makeQuery(id+"F5.imprint","IMPRINT",EDGE,{"derivedFrom":sQuery(id+"F5.wireOp",EDGE,"E55")}),1.0]])]});
            extrude(context, id + "F6", {"entities" : qUnion([Q0, Q1, Q2, Q3, Q4, Q5, Q6, Q7, Q8, Q9, Q10, Q11, Q12, Q13, Q14, Q15, Q16, Q17, Q18, Q19, Q20, Q21, Q22, Q23, Q24, Q25, Q26, Q27, Q28, Q29, Q30, Q31, Q32, Q33, Q34, Q35, Q36, Q37, Q38, Q39, Q40, Q41, Q42, Q43, Q44, Q45, Q46, Q47]), "operationType" : NewBodyOperationType.REMOVE, "oppositeDirection" : true, "depth" : 25 * mm});
        }
        {
            var Q0;
            Q0=makeQuery(id+"F2.opExtrude","SWEPT_FACE",FACE,{"disambiguationData":[OSD([sQuery(id+"F0.wireOp",EDGE,"E0.bottom")])]});
            var sketch = newSketch(context, id + "F7", { "sketchPlane" : qUnion([Q0])});
            skLineSegment(sketch, "E57.bottom", {"start": v(-6.58, 57) * mm, "end": v(9.42, 57) * mm});
            skLineSegment(sketch, "E57.top", {"start": v(-6.58, 35) * mm, "end": v(9.42, 35) * mm});
            skLineSegment(sketch, "E57.left", {"start": v(-6.58, 57) * mm, "end": v(-6.58, 35) * mm});
            skLineSegment(sketch, "E57.right", {"start": v(9.42, 57) * mm, "end": v(9.42, 35) * mm});
            skLineSegment(sketch, "E58.bottom", {"start": v(-5.08, 55.5) * mm, "end": v(7.92, 55.5) * mm});
            skLineSegment(sketch, "E58.top", {"start": v(-5.08, 36.5) * mm, "end": v(7.92, 36.5) * mm});
            skLineSegment(sketch, "E58.left", {"start": v(-5.08, 55.5) * mm, "end": v(-5.08, 36.5) * mm});
            skLineSegment(sketch, "E58.right", {"start": v(7.92, 55.5) * mm, "end": v(7.92, 36.5) * mm});
            skSolve(sketch);
        }
        {
            var Q0;
            Q0=makeQuery(id+"F7.imprint","IMPRINT",FACE,{"disambiguationData":[TD([[makeQuery(id+"F7.imprint","IMPRINT",EDGE,{"derivedFrom":sQuery(id+"F7.wireOp",EDGE,"E58.bottom")}),-1.0]])]});
            extrude(context, id + "F8", {"entities" : qUnion([Q0]), "operationType" : NewBodyOperationType.REMOVE, "oppositeDirection" : true, "depth" : 25 * mm});
        }
        {
            var Q0;
            Q0=makeQuery(id+"F7.imprint","IMPRINT",FACE,{"disambiguationData":[TD([[makeQuery(id+"F7.imprint","IMPRINT",EDGE,{"derivedFrom":sQuery(id+"F7.wireOp",EDGE,"E57.bottom")}),-1.0]])]});
            extrude(context, id + "F9", {"entities" : qUnion([Q0]), "operationType" : NewBodyOperationType.REMOVE, "oppositeDirection" : true, "depth" : 2.5 * mm});
        }
    });
